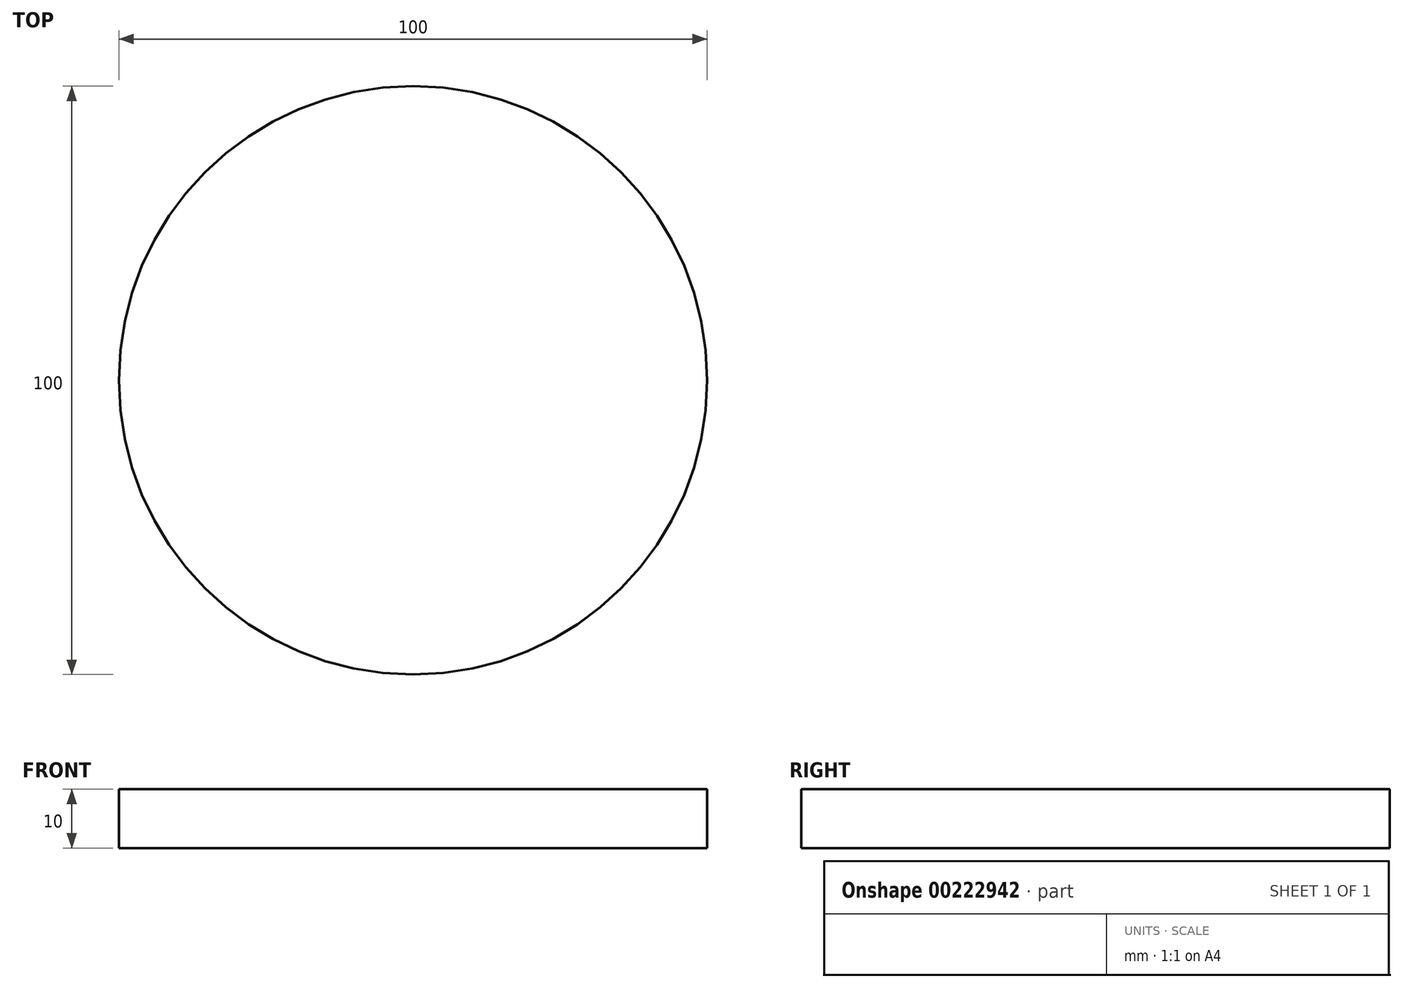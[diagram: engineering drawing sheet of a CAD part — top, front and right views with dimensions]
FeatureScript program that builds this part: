
annotation { "Feature Type Name" : "Feature", "Feature Type Description" : "" }
export const myFeature = defineFeature(function(context is Context, id is Id, definition is map)
    precondition{}
    {
        {
            var Q0;
            Q0=qCreatedBy(makeId("Top.planeOp"),FACE);
            var sketch = newSketch(context, id + "F0", { "sketchPlane" : qUnion([Q0])});
            skCircle(sketch, "E0", {"center": v(0, 0) * mm, "radius": 50 * mm});
            skSolve(sketch);
        }
        {
            var Q0;
            Q0=makeQuery(id+"F0.imprint","IMPRINT",FACE,{"disambiguationData":[TD([[makeQuery(id+"F0.imprint","IMPRINT",EDGE,{"derivedFrom":sQuery(id+"F0.wireOp",EDGE,"E0")}),1.0]])]});
            extrude(context, id + "F1", {"entities" : qUnion([Q0]), "depth" : 10 * mm});
        }
    });
